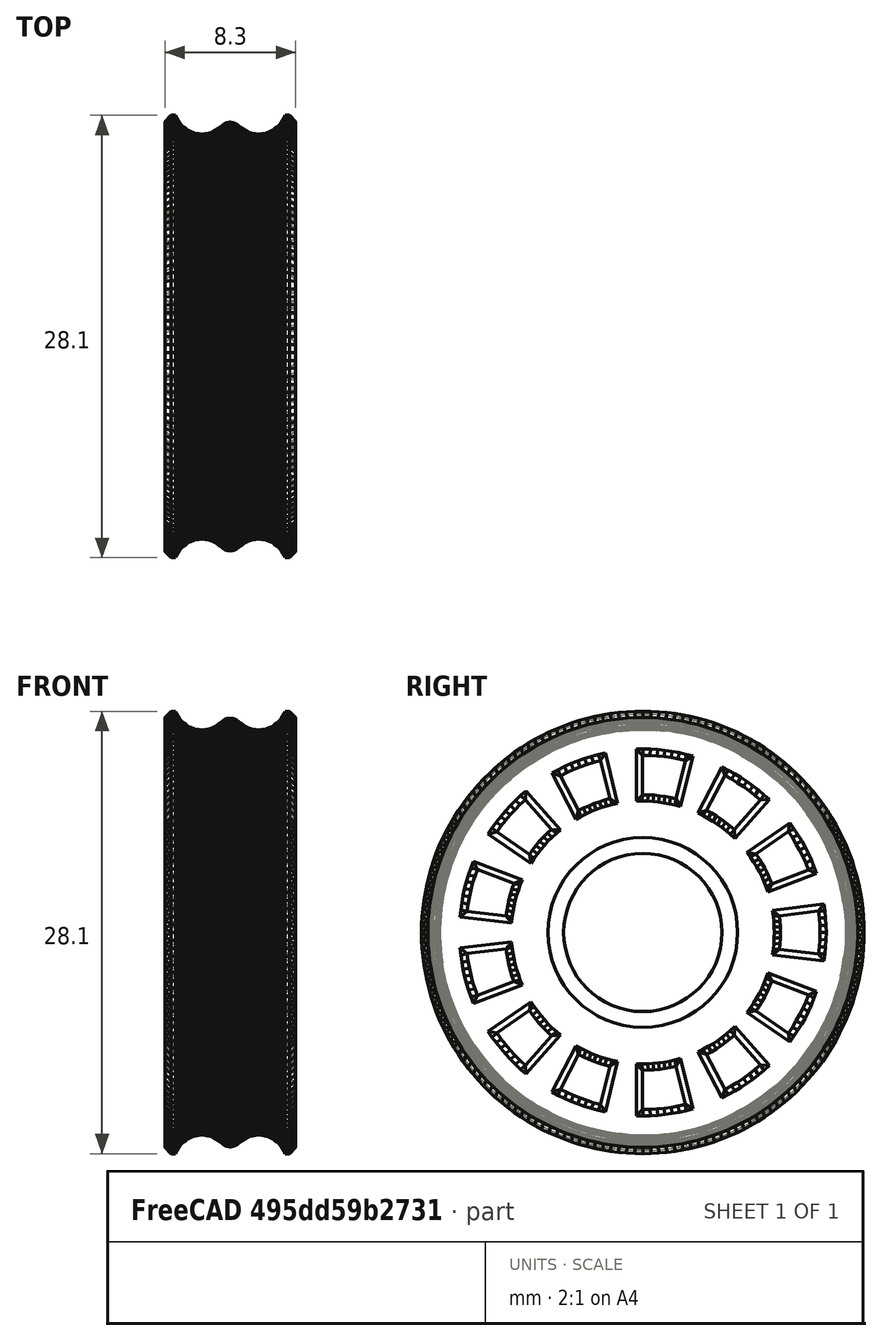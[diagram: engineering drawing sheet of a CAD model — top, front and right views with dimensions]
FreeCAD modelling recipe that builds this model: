
FCSTD DOCUMENT  (FreeCAD 0.20R29177 +233 (Git))
Label: scrollwheel_with_bearing
License: All rights reserved
LicenseURL: http://en.wikipedia.org/wiki/All_rights_reserved
objects: Part::Feature×2, Mesh::Feature×1, Part::Refine×1, PartDesign::FeatureBase×1, Sketcher::SketchObject×1, PartDesign::Pocket×1, PartDesign::Chamfer×1, PartDesign::Body×1
note: 10 computed .brp shape members not serialized (recipe doc carries the construction recipe); baked Part::Feature solids carry a one-line shape summary decoded from their .brp

FEATURE [Mesh::Feature] ScrollWheel
FEATURE [Part::Feature] ScrollWheel001
  shape: bbox 8.3 x 28.1 x 28.1 mm, 27432 faces, 0 solids (baked)
FEATURE [Part::Feature] ScrollWheel001_solid  label="ScrollWheel001 (Solid)"
  shape: bbox 8.3 x 28.1 x 28.1 mm, 27432 faces (baked)
FEATURE [Part::Refine] ScrollWheel001_solid001  label="ScrollWheel001 (Solid)001"
  Source = -> ScrollWheel001_solid
FEATURE [PartDesign::FeatureBase] BaseFeature
  BaseFeature = -> ScrollWheel001_solid001
FEATURE [Sketcher::SketchObject] Sketch
  FullyConstrained = true
  MapMode = 5
  Placement = pos=(8.3,0,0) rot=(0.57735,0.57735,0.57735;2.0944rad)
  Support = -> [BaseFeature]
  sketch-geometry (1):
    g0: Circle CenterX=0 CenterY=0 CenterZ=0 NormalX=0 NormalY=0 NormalZ=1 AngleXU=0 Radius=5.025
  constraints (2):
    c: Coincident(g0,g-1)
    c: Diameter(g0) = 10.05
FEATURE [PartDesign::Pocket] Pocket
  BaseFeature = -> BaseFeature
  Direction = (-1,0,0)
  Length = 0
  Length2 = 5
  Profile = -> Sketch
  ReferenceAxis = -> Sketch [N_Axis]
  Type = 3
  UpToFace = -> BaseFeature [Face24934]
FEATURE [PartDesign::Chamfer] Chamfer
  Angle = 45
  Base = -> Pocket [Edge1034,Edge1789]
  BaseFeature = -> Pocket
  ChamferType = 0
  FlipDirection = false
  Size = 1
  Size2 = 1
  SupportTransform = false
  UseAllEdges = false
FEATURE [PartDesign::Body] Body
  BaseFeature = -> ScrollWheel001_solid001
  Group = -> [BaseFeature,Sketch,Pocket,Chamfer]
  Origin = -> Origin
  Tip = -> Chamfer
